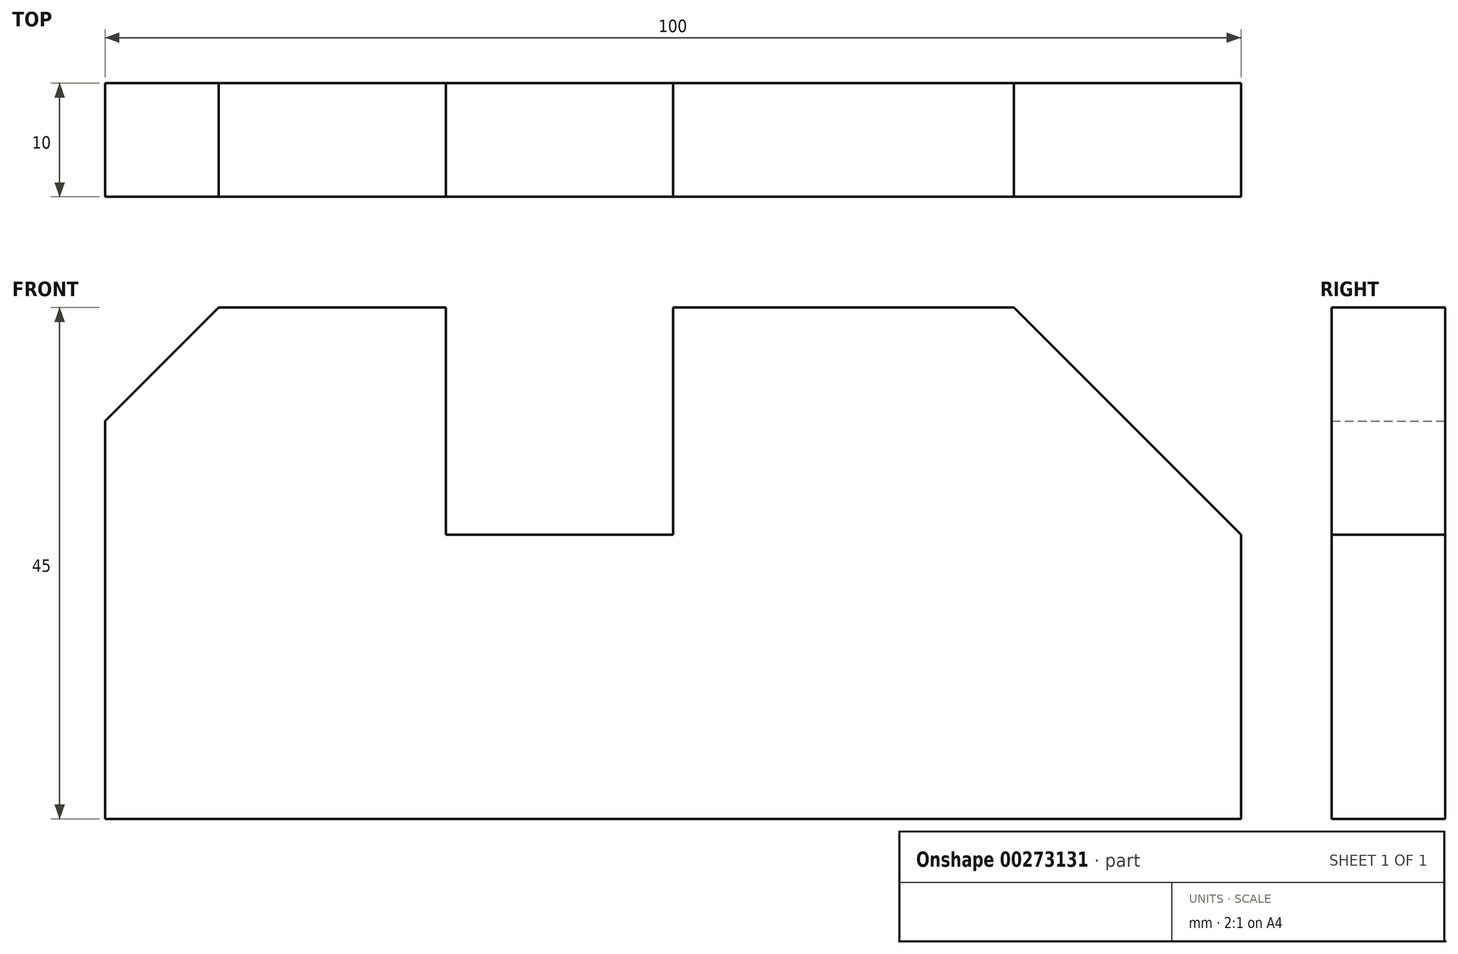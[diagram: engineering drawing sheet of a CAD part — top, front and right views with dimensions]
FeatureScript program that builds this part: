
annotation { "Feature Type Name" : "Feature", "Feature Type Description" : "" }
export const myFeature = defineFeature(function(context is Context, id is Id, definition is map)
    precondition{}
    {
        {
            var Q0;
            Q0=qCreatedBy(makeId("Front.planeOp"),FACE);
            var sketch = newSketch(context, id + "F0", { "sketchPlane" : qUnion([Q0])});
            skLineSegment(sketch, "E0", {"start": v(0, 0) * mm, "end": v(100, 0) * mm});
            skLineSegment(sketch, "E1", {"start": v(0, 0) * mm, "end": v(0, 35) * mm});
            skLineSegment(sketch, "E2", {"start": v(0, 35) * mm, "end": v(10, 45) * mm});
            skLineSegment(sketch, "E3", {"start": v(10, 45) * mm, "end": v(30, 45) * mm});
            skLineSegment(sketch, "E4", {"start": v(30, 45) * mm, "end": v(30, 25) * mm});
            skLineSegment(sketch, "E5", {"start": v(30, 25) * mm, "end": v(50, 25) * mm});
            skLineSegment(sketch, "E6", {"start": v(50, 25) * mm, "end": v(50, 45) * mm});
            skLineSegment(sketch, "E7", {"start": v(50, 45) * mm, "end": v(80, 45) * mm});
            skLineSegment(sketch, "E8", {"start": v(80, 45) * mm, "end": v(100, 25) * mm});
            skLineSegment(sketch, "E9", {"start": v(100, 25) * mm, "end": v(100, 0) * mm});
            skSolve(sketch);
        }
        {
            var Q0;
            Q0=makeQuery(id+"F0.imprint","IMPRINT",FACE,{"disambiguationData":[TD([[makeQuery(id+"F0.imprint","IMPRINT",EDGE,{"derivedFrom":sQuery(id+"F0.wireOp",EDGE,"E0")}),1.0]])]});
            extrude(context, id + "F1", {"entities" : qUnion([Q0]), "depth" : 10 * mm});
        }
    });
